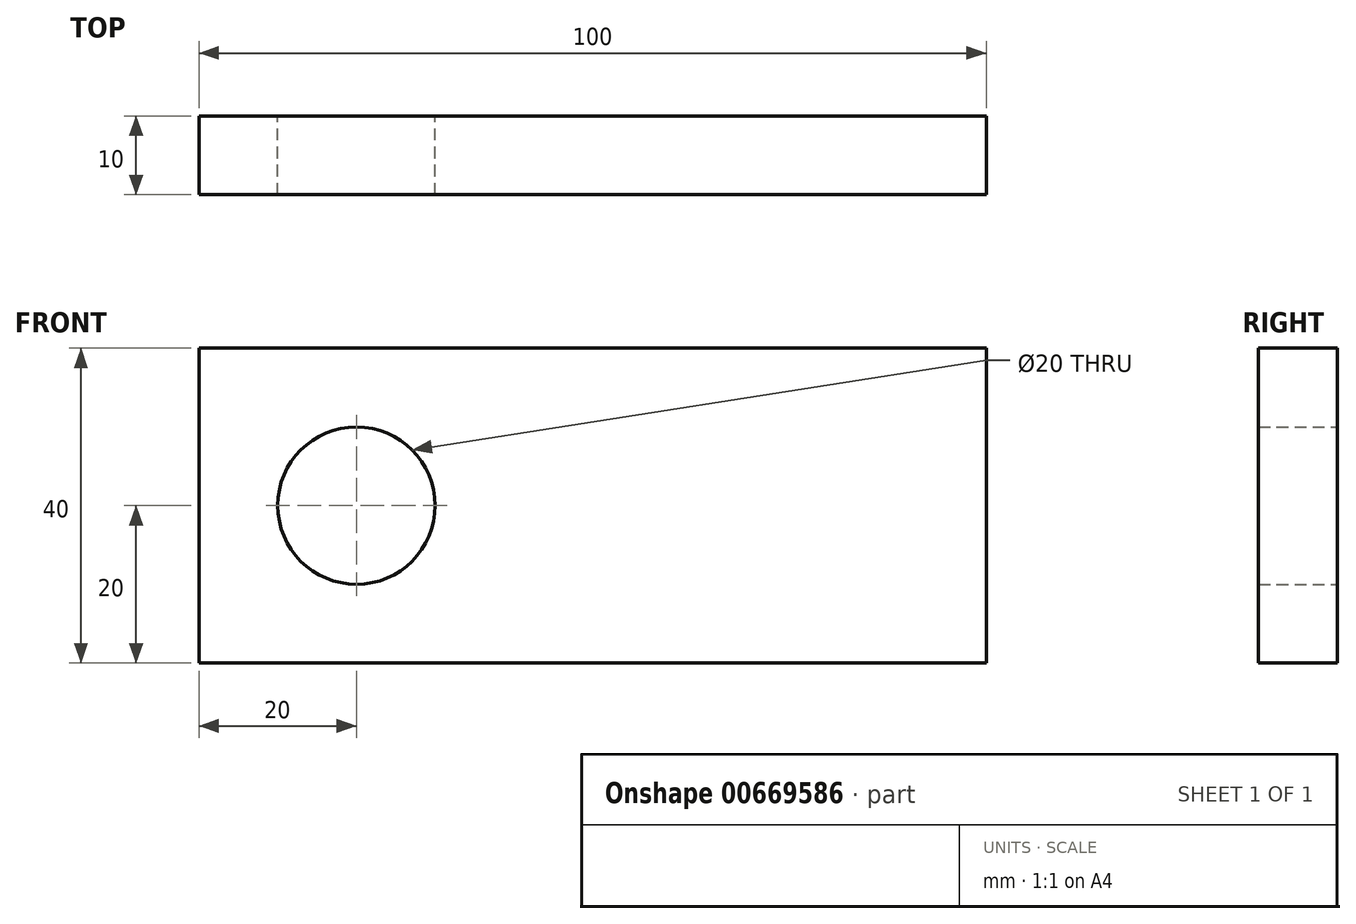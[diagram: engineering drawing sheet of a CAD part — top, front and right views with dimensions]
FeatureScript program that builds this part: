
annotation { "Feature Type Name" : "Feature", "Feature Type Description" : "" }
export const myFeature = defineFeature(function(context is Context, id is Id, definition is map)
    precondition{}
    {
        {
            var Q0;
            Q0=qCreatedBy(makeId("Front.planeOp"),FACE);
            var sketch = newSketch(context, id + "F0", { "sketchPlane" : qUnion([Q0])});
            skLineSegment(sketch, "E0.bottom", {"start": v(0, 40) * mm, "end": v(100, 40) * mm});
            skLineSegment(sketch, "E0.top", {"start": v(0, 0) * mm, "end": v(100, 0) * mm});
            skLineSegment(sketch, "E0.left", {"start": v(0, 40) * mm, "end": v(0, 0) * mm});
            skLineSegment(sketch, "E0.right", {"start": v(100, 40) * mm, "end": v(100, 0) * mm});
            skCircle(sketch, "E1", {"center": v(20, 20) * mm, "radius": 10 * mm});
            skSolve(sketch);
        }
        {
            var Q0;
            Q0=makeQuery(id+"F0.imprint","IMPRINT",FACE,{"disambiguationData":[TD([[makeQuery(id+"F0.imprint","IMPRINT",EDGE,{"derivedFrom":sQuery(id+"F0.wireOp",EDGE,"E0.bottom")}),-1.0]])]});
            extrude(context, id + "F1", {"entities" : qUnion([Q0]), "depth" : 10 * mm, "offsetDistance" : 25 * mm});
        }
    });
